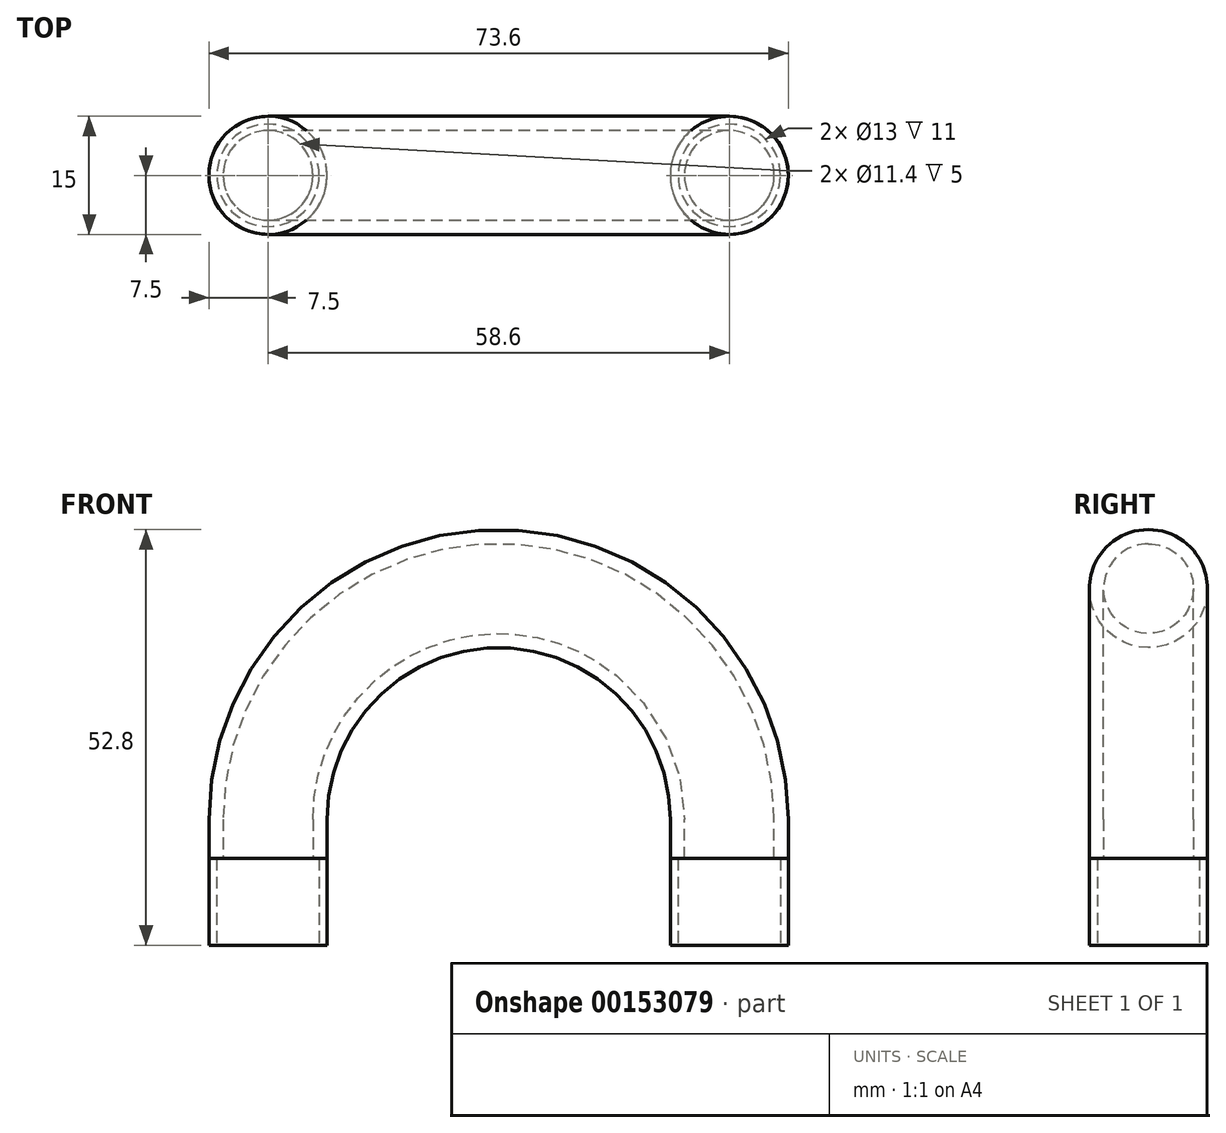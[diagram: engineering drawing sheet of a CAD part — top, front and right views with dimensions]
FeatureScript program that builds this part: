
annotation { "Feature Type Name" : "Feature", "Feature Type Description" : "" }
export const myFeature = defineFeature(function(context is Context, id is Id, definition is map)
    precondition{}
    {
        {
            var Q0;
            Q0=qCreatedBy(makeId("Front.planeOp"),FACE);
            var sketch = newSketch(context, id + "F0", { "sketchPlane" : qUnion([Q0])});
            skLineSegment(sketch, "E0", {"start": v(-29.3, 0) * mm, "end": v(-29.3, 5) * mm});
            skLineSegment(sketch, "E1", {"start": v(29.3, 0) * mm, "end": v(29.3, 5) * mm});
            skArc(sketch, "E2", {"start": v(-29.3, 5) * mm, "mid": v(0, 34.3) * mm, "end": v(29.3, 5) * mm});
            skSolve(sketch);
        }
        {
            var Q0;
            Q0=qCreatedBy(makeId("Top.planeOp"),FACE);
            var sketch = newSketch(context, id + "F1", { "sketchPlane" : qUnion([Q0])});
            skCircle(sketch, "E3", {"center": v(29.3, 0) * mm, "radius": 5.7 * mm});
            skCircle(sketch, "E4", {"center": v(29.3, 0) * mm, "radius": 7.5 * mm});
            skSolve(sketch);
        }
        {
            var Q0;
            Q0=qCreatedBy(makeId("Front.planeOp"),FACE);
            var sketch = newSketch(context, id + "F2", { "sketchPlane" : qUnion([Q0])});
            skLineSegment(sketch, "E5", {"start": v(-29.3, 0) * mm, "end": v(-29.3, -11) * mm});
            skSolve(sketch);
        }
        {
            var Q0;
            Q0=qCreatedBy(makeId("Front.planeOp"),FACE);
            var sketch = newSketch(context, id + "F3", { "sketchPlane" : qUnion([Q0])});
            skLineSegment(sketch, "E6", {"start": v(29.3, 0) * mm, "end": v(29.3, -11) * mm});
            skSolve(sketch);
        }
        {
            var Q0;
            Q0=qCreatedBy(makeId("Top.planeOp"),FACE);
            var sketch = newSketch(context, id + "F4", { "sketchPlane" : qUnion([Q0])});
            skCircle(sketch, "E7", {"center": v(29.3, 0) * mm, "radius": 7.5 * mm});
            skCircle(sketch, "E8", {"center": v(29.3, 0) * mm, "radius": 6.5 * mm});
            skSolve(sketch);
        }
        {
            var Q0;
            Q0=qCreatedBy(makeId("Top.planeOp"),FACE);
            var sketch = newSketch(context, id + "F5", { "sketchPlane" : qUnion([Q0])});
            skCircle(sketch, "E9", {"center": v(-29.3, 0) * mm, "radius": 7.5 * mm});
            skCircle(sketch, "E10", {"center": v(-29.3, 0) * mm, "radius": 6.5 * mm});
            skSolve(sketch);
        }
        {
            var Q0;
            Q0=makeQuery(id+"F1.imprint","IMPRINT",FACE,{"disambiguationData":[TD([[makeQuery(id+"F1.imprint","IMPRINT",EDGE,{"derivedFrom":sQuery(id+"F1.wireOp",EDGE,"E3")}),-1.0]])]});
            var Q1;
            Q1 = qConstructionFilter(qBodyType(qCreatedBy(id + "F0" ,EDGE), BodyType.WIRE), ConstructionObject.NO);
            sweep(context, id + "F6", {"profiles" : qUnion([Q0]), "path" : qUnion([Q1])});
        }
        {
            var Q0;
            Q0=makeQuery(id+"F4.imprint","IMPRINT",FACE,{"disambiguationData":[TD([[makeQuery(id+"F4.imprint","IMPRINT",EDGE,{"derivedFrom":sQuery(id+"F4.wireOp",EDGE,"E7")}),1.0]])]});
            var Q1;
            Q1=sQuery(id+"F3.wireOp",EDGE,"E6");
            sweep(context, id + "F7", {"profiles" : qUnion([Q0]), "path" : qUnion([Q1])});
        }
        {
            var Q0;
            Q0=makeQuery(id+"F5.imprint","IMPRINT",FACE,{"disambiguationData":[TD([[makeQuery(id+"F5.imprint","IMPRINT",EDGE,{"derivedFrom":sQuery(id+"F5.wireOp",EDGE,"E9")}),1.0]])]});
            var Q1;
            Q1=sQuery(id+"F2.wireOp",EDGE,"E5");
            sweep(context, id + "F8", {"profiles" : qUnion([Q0]), "path" : qUnion([Q1])});
        }
    });
